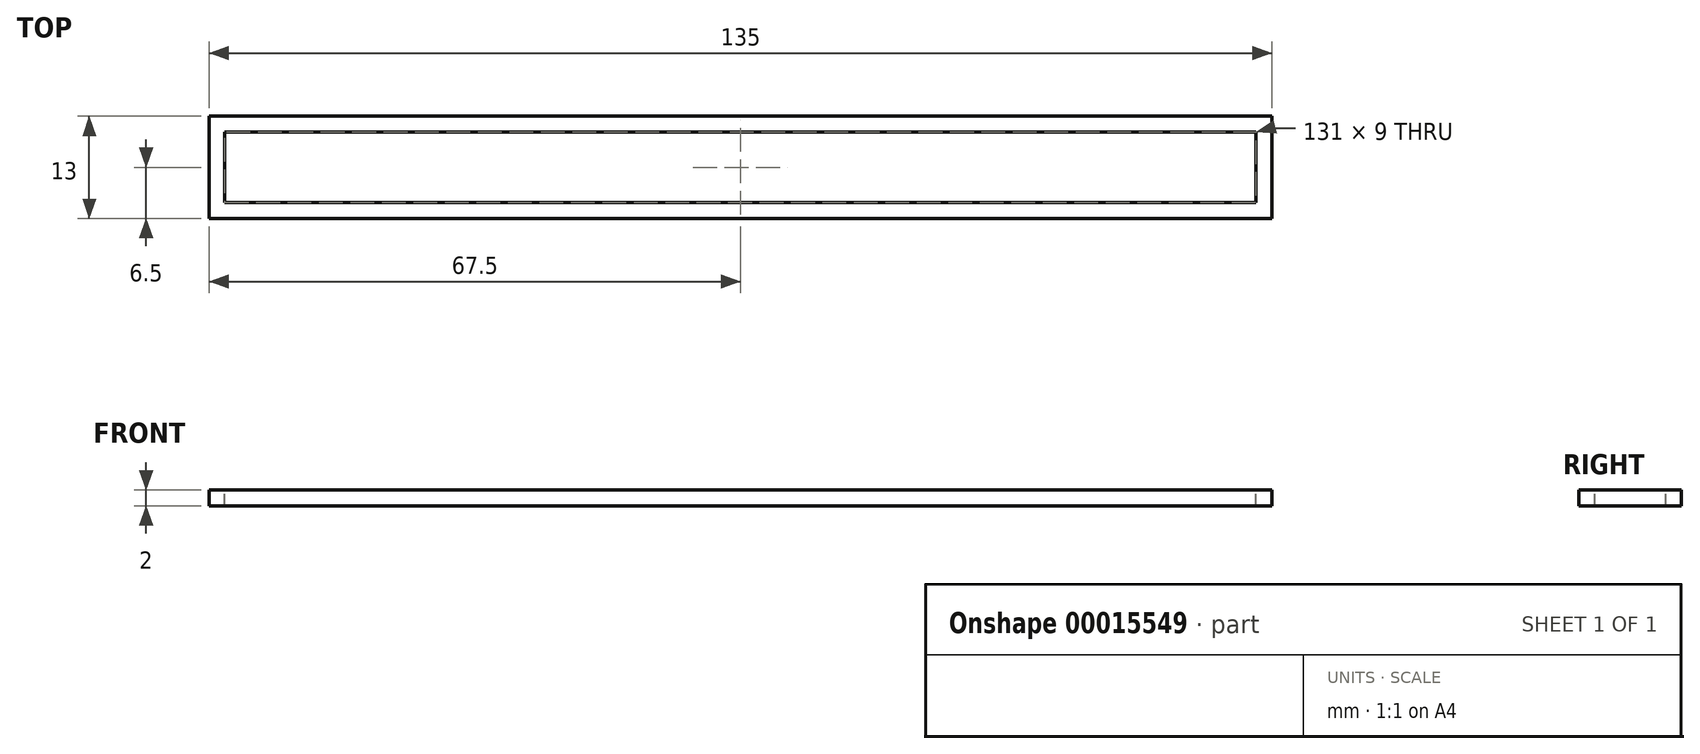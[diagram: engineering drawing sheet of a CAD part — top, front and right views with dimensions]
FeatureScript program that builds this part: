
annotation { "Feature Type Name" : "Feature", "Feature Type Description" : "" }
export const myFeature = defineFeature(function(context is Context, id is Id, definition is map)
    precondition{}
    {
        {
            var Q0;
            Q0=qCreatedBy(makeId("Right.planeOp"),FACE);
            var sketch = newSketch(context, id + "F0", { "sketchPlane" : qUnion([Q0])});
            skLineSegment(sketch, "E0.bottom", {"start": v(0, 0) * mm, "end": v(13, 0) * mm});
            skLineSegment(sketch, "E0.top", {"start": v(0, 2) * mm, "end": v(13, 2) * mm});
            skLineSegment(sketch, "E0.left", {"start": v(0, 0) * mm, "end": v(0, 2) * mm});
            skLineSegment(sketch, "E0.right", {"start": v(13, 0) * mm, "end": v(13, 2) * mm});
            skPoint(sketch, "E1.visualSharp", {"position": v(13, 2) * mm});
            skSolve(sketch);
        }
        {
            var Q0;
            Q0=makeQuery(id+"F0.imprint","IMPRINT",FACE,{"disambiguationData":[TD([[makeQuery(id+"F0.imprint","IMPRINT",EDGE,{"derivedFrom":sQuery(id+"F0.wireOp",EDGE,"E0.bottom")}),1.0]])]});
            extrude(context, id + "F1", {"entities" : qUnion([Q0]), "depth" : 135 * mm});
        }
        {
            var Q0;
            Q0=makeQuery(id+"F1.opExtrude","SWEPT_FACE",FACE,{"disambiguationData":[OSD([sQuery(id+"F0.wireOp",EDGE,"E0.top")])]});
            var sketch = newSketch(context, id + "F2", { "sketchPlane" : qUnion([Q0])});
            skLineSegment(sketch, "E2.bottom", {"start": v(2, 2) * mm, "end": v(133, 2) * mm});
            skLineSegment(sketch, "E2.top", {"start": v(2, 11) * mm, "end": v(133, 11) * mm});
            skLineSegment(sketch, "E2.left", {"start": v(2, 2) * mm, "end": v(2, 11) * mm});
            skLineSegment(sketch, "E2.right", {"start": v(133, 2) * mm, "end": v(133, 11) * mm});
            skSolve(sketch);
        }
        {
            var Q0;
            Q0 = qSketchRegion(id + "F2", true);
            extrude(context, id + "F3", {"entities" : qUnion([Q0]), "operationType" : NewBodyOperationType.REMOVE, "endBound" : BoundingType.UP_TO_NEXT, "oppositeDirection" : true, "depth" : 25 * mm});
        }
    });
